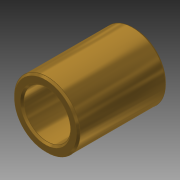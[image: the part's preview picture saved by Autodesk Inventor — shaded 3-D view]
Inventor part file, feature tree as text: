
AUTODESK INVENTOR PART (.ipt)
format: ipt  version: 2014 SP1 (Build 180222100, 222)  size: 102,400 bytes
history: native  units: in
note: dims shown in document units (in); Inventor stores cm internally (conversion verified against a paired STEP export)
features: extrude x1, chamfer x1, sketch x1
ambient origin geometry x8: Origin, YZ Plane, XZ Plane, XY Plane, X Axis, Y Axis, Z Axis, Center Point
bodies: Solid1 (feature_tree)
feature tree (3):
  extrude  "Extrusion1"  Depth=0.125in
  chamfer  "Chamfer1"  Distance=0.475in
  sketch  "Sketch1"  dims[d0=0.35in d1=0.25in d2=0.475in d3=0.0in d4=0.01in d5=0.125in d6=45.0deg]
